# Revit family: Doors_Industrial_Wayne-Dalton_Advanced-Rolling-Door-System-Model-800-ADV
name_source: partatom
category: Specialty Equipment
units: mm (PartAtom-declared; Revit-internal decimal feet)

## family parameters
Always vertical = Yes
Classification Number = 23.30.10.21.34
Cut with Voids When Loaded = Yes
Enable Cutting in Views = No
Host = Wall
Maintain Annotation Orientation = No
Part Type = Normal
Room Calculation Point = No
Round Connector Dimension = Use Diameter
Shared = No

## types (6) — shared parameters
Chain Hoist or Manual = No
Connector Array = 3
Connector Array Distance = 0"
Current = 20 A
Default Elevation = 0"
Description = Model 800 ADV Advanced Rolling Door System
Finish Material = Finish - Wayne Dalton - Black
Frequency = 60 Hz
Manufacturer = Wayne Dalton
Model = 800 ADV
Operator Visibility = Yes
Powder Coat (Note) = Wayne Dalton also offers approximately 200 RAL powder coat options to complement the exterior colors of a building.
Power Factor = 1
Product Guid = 0b55cba0-5740-4beb-a360-9fda8dc8a982
Product Page URL = https://www.wayne-dalton.com
Product data url = https://www.bimobject.com
URL = https://www.wayne-dalton.com
Wall Closure = By host

## per-type parameters (varying)
| type | Apparent Load Phase 1 | Apparent Load Phase 2 | Apparent Load Phase 3 | Number of Poles | Voltage |
| 208 volts, one phase, 60 Hz (208-240V range) | 4160 VA | 0 VA | 0 VA | 1 | 208 V |
| 230 volts, three phase, 60 Hz (220-240V range) | 2656 VA | 2656 VA | 2656 VA | 3 | 230 V |
| 208 volts, three phase, 60 Hz (208-240V range) | 2402 VA | 2402 VA | 2402 VA | 3 | 208 V |
| 460 volts, three phase, 60 Hz (440-480V range) | 5312 VA | 5312 VA | 5312 VA | 3 | 460 V |
| 220 volts, one phase, 60 Hz (220-240V range) | 4400 VA | 0 VA | 0 VA | 1 | 220 V |
| 575 volts, three phase, 60 Hz | 5312 VA | 5312 VA | 5312 VA | 3 | 460 V |

## geometry (parser evidence)
native form markers: Sweep x10
no freeform markers — native parametric forms only
